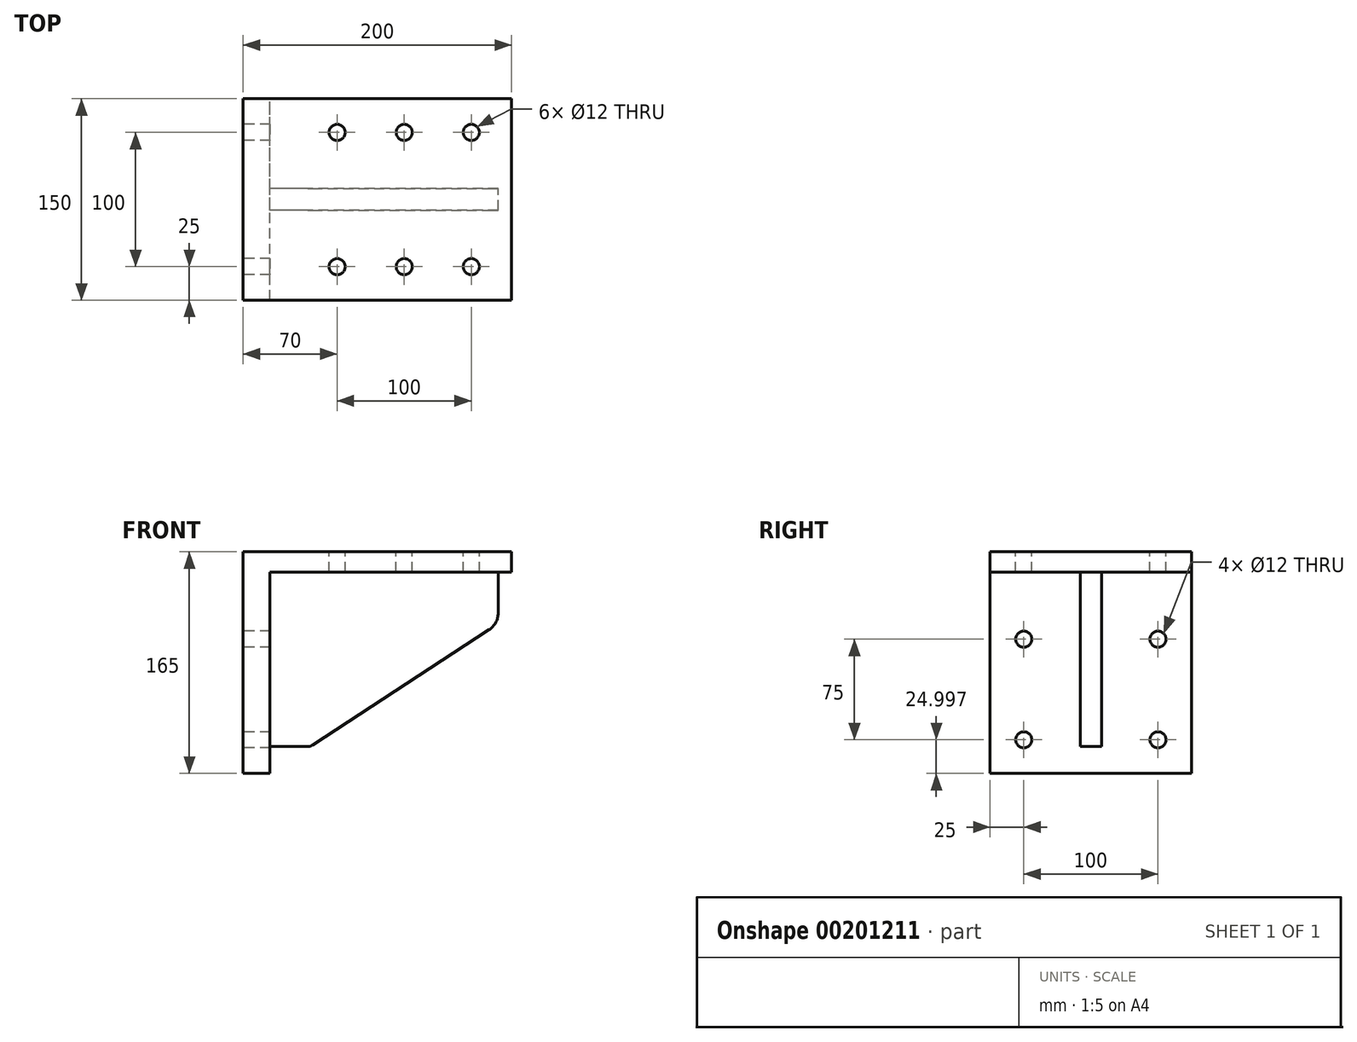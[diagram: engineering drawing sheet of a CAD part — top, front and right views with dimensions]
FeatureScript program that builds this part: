
annotation { "Feature Type Name" : "Feature", "Feature Type Description" : "" }
export const myFeature = defineFeature(function(context is Context, id is Id, definition is map)
    precondition{}
    {
        {
            var Q0;
            Q0=qCreatedBy(makeId("Front.planeOp"),FACE);
            var sketch = newSketch(context, id + "F0", { "sketchPlane" : qUnion([Q0])});
            skLineSegment(sketch, "E0", {"start": v(-75.86, -70.64) * mm, "end": v(-95.86, -70.64) * mm});
            skLineSegment(sketch, "E1", {"start": v(-95.86, -70.64) * mm, "end": v(-95.86, 94.36) * mm});
            skLineSegment(sketch, "E2", {"start": v(-95.86, 94.36) * mm, "end": v(104.14, 94.36) * mm});
            skLineSegment(sketch, "E3", {"start": v(104.14, 94.36) * mm, "end": v(104.14, 79.36) * mm});
            skLineSegment(sketch, "E4", {"start": v(104.14, 79.36) * mm, "end": v(-75.86, 79.36) * mm});
            skLineSegment(sketch, "E5", {"start": v(-75.86, 79.36) * mm, "end": v(-75.86, -70.64) * mm});
            skSolve(sketch);
        }
        {
            var Q0;
            Q0 = qSketchRegion(id + "F0", true);
            extrude(context, id + "F1", {"entities" : qUnion([Q0]), "depth" : 150 * mm});
        }
        {
            var Q0;
            Q0=makeQuery(id+"F1.opExtrude","SWEPT_FACE",FACE,{"disambiguationData":[OSD([sQuery(id+"F0.wireOp",EDGE,"E5")])]});
            var sketch = newSketch(context, id + "F2", { "sketchPlane" : qUnion([Q0])});
            skLineSegment(sketch, "E6", {"start": v(-83, -50.64) * mm, "end": v(-67, -50.64) * mm});
            skLineSegment(sketch, "E7", {"start": v(-67, -50.64) * mm, "end": v(-67, 79.36) * mm});
            skLineSegment(sketch, "E8", {"start": v(-67, 79.36) * mm, "end": v(-83, 79.36) * mm});
            skLineSegment(sketch, "E9", {"start": v(-83, 79.36) * mm, "end": v(-83, -50.64) * mm});
            skSolve(sketch);
        }
        {
            var Q0;
            Q0=makeQuery(id+"F2.imprint","IMPRINT",FACE,{"disambiguationData":[TD([[makeQuery(id+"F2.imprint","IMPRINT",EDGE,{"derivedFrom":sQuery(id+"F2.wireOp",EDGE,"E6")}),1.0]])]});
            extrude(context, id + "F3", {"entities" : qUnion([Q0]), "operationType" : NewBodyOperationType.ADD, "depth" : 170 * mm});
        }
        {
            var Q0;
            Q0=makeQuery(id+"F3.opExtrude","SWEPT_FACE",FACE,{"disambiguationData":[OSD([sQuery(id+"F2.wireOp",EDGE,"E9")])]});
            var sketch = newSketch(context, id + "F4", { "sketchPlane" : qUnion([Q0])});
            skLineSegment(sketch, "E10", {"start": v(-75.86, -50.64) * mm, "end": v(-47.65, -50.64) * mm});
            skLineSegment(sketch, "E11", {"start": v(94.14, 79.36) * mm, "end": v(94.14, 48.87) * mm});
            skLineSegment(sketch, "E12", {"start": v(-44.37, -49.67) * mm, "end": v(87.34, 36.31) * mm});
            skArc(sketch, "E13", {"start": v(87.34, 36.31) * mm, "mid": v(92.33, 41.73) * mm, "end": v(94.14, 48.87) * mm});
            skPoint(sketch, "E14.visualSharp", {"position": v(-45.86, -50.64) * mm});
            skArc(sketch, "E14.filletArc", {"start": v(-47.65, -50.64) * mm, "mid": v(-45.93, -50.4) * mm, "end": v(-44.37, -49.67) * mm});
            skLineSegment(sketch, "E15", {"start": v(-75.86, -50.64) * mm, "end": v(-75.86, -70.64) * mm});
            skLineSegment(sketch, "E16", {"start": v(-75.86, -70.64) * mm, "end": v(124.14, -70.64) * mm});
            skLineSegment(sketch, "E17", {"start": v(124.14, -70.64) * mm, "end": v(124.14, 79.36) * mm});
            skLineSegment(sketch, "E18", {"start": v(124.14, 79.36) * mm, "end": v(94.14, 79.36) * mm});
            skSolve(sketch);
        }
        {
            var Q0;
            Q0=makeQuery(id+"F4.imprint","IMPRINT",FACE,{"disambiguationData":[TD([[makeQuery(id+"F4.imprint","IMPRINT",EDGE,{"derivedFrom":sQuery(id+"F4.wireOp",EDGE,"E12")}),-1.0]])]});
            extrude(context, id + "F5", {"entities" : qUnion([Q0]), "operationType" : NewBodyOperationType.REMOVE, "oppositeDirection" : true, "depth" : 16 * mm});
        }
        {
            var Q0;
            Q0=makeQuery(id+"F1.opExtrude","SWEPT_FACE",FACE,{"disambiguationData":[OSD([sQuery(id+"F0.wireOp",EDGE,"E2")])]});
            var sketch = newSketch(context, id + "F6", { "sketchPlane" : qUnion([Q0])});
            skCircle(sketch, "E19", {"center": v(-25.86, -25) * mm, "radius": 6 * mm});
            skCircle(sketch, "E20", {"center": v(24.14, -25) * mm, "radius": 6 * mm});
            skCircle(sketch, "E21", {"center": v(74.14, -25) * mm, "radius": 6 * mm});
            skCircle(sketch, "E22", {"center": v(74.14, -125) * mm, "radius": 6 * mm});
            skCircle(sketch, "E23", {"center": v(24.14, -125) * mm, "radius": 6 * mm});
            skCircle(sketch, "E24", {"center": v(-25.86, -125) * mm, "radius": 6 * mm});
            skSolve(sketch);
        }
        {
            var Q0;
            Q0 = qSketchRegion(id + "F6", true);
            extrude(context, id + "F7", {"entities" : qUnion([Q0]), "operationType" : NewBodyOperationType.REMOVE, "oppositeDirection" : true, "depth" : 15 * mm});
        }
        {
            var Q0;
            Q0=makeQuery(id+"F1.opExtrude","SWEPT_FACE",FACE,{"disambiguationData":[OSD([sQuery(id+"F0.wireOp",EDGE,"E1")])]});
            var sketch = newSketch(context, id + "F8", { "sketchPlane" : qUnion([Q0])});
            skCircle(sketch, "E25", {"center": v(125, 29.36) * mm, "radius": 6 * mm});
            skCircle(sketch, "E26", {"center": v(125, -45.64) * mm, "radius": 6 * mm});
            skCircle(sketch, "E27", {"center": v(25, -45.64) * mm, "radius": 6 * mm});
            skCircle(sketch, "E28", {"center": v(25, 29.36) * mm, "radius": 6 * mm});
            skSolve(sketch);
        }
        {
            var Q0;
            Q0=makeQuery(id+"F8.imprint","IMPRINT",FACE,{"disambiguationData":[TD([[makeQuery(id+"F8.imprint","IMPRINT",EDGE,{"derivedFrom":sQuery(id+"F8.wireOp",EDGE,"E25")}),1.0]])]});
            var Q1;
            Q1=makeQuery(id+"F8.imprint","IMPRINT",FACE,{"disambiguationData":[TD([[makeQuery(id+"F8.imprint","IMPRINT",EDGE,{"derivedFrom":sQuery(id+"F8.wireOp",EDGE,"E26")}),1.0]])]});
            var Q2;
            Q2=makeQuery(id+"F8.imprint","IMPRINT",FACE,{"disambiguationData":[TD([[makeQuery(id+"F8.imprint","IMPRINT",EDGE,{"derivedFrom":sQuery(id+"F8.wireOp",EDGE,"E27")}),1.0]])]});
            var Q3;
            Q3=makeQuery(id+"F8.imprint","IMPRINT",FACE,{"disambiguationData":[TD([[makeQuery(id+"F8.imprint","IMPRINT",EDGE,{"derivedFrom":sQuery(id+"F8.wireOp",EDGE,"E28")}),1.0]])]});
            extrude(context, id + "F9", {"entities" : qUnion([Q0, Q1, Q2, Q3]), "operationType" : NewBodyOperationType.REMOVE, "oppositeDirection" : true, "depth" : 20 * mm});
        }
    });
